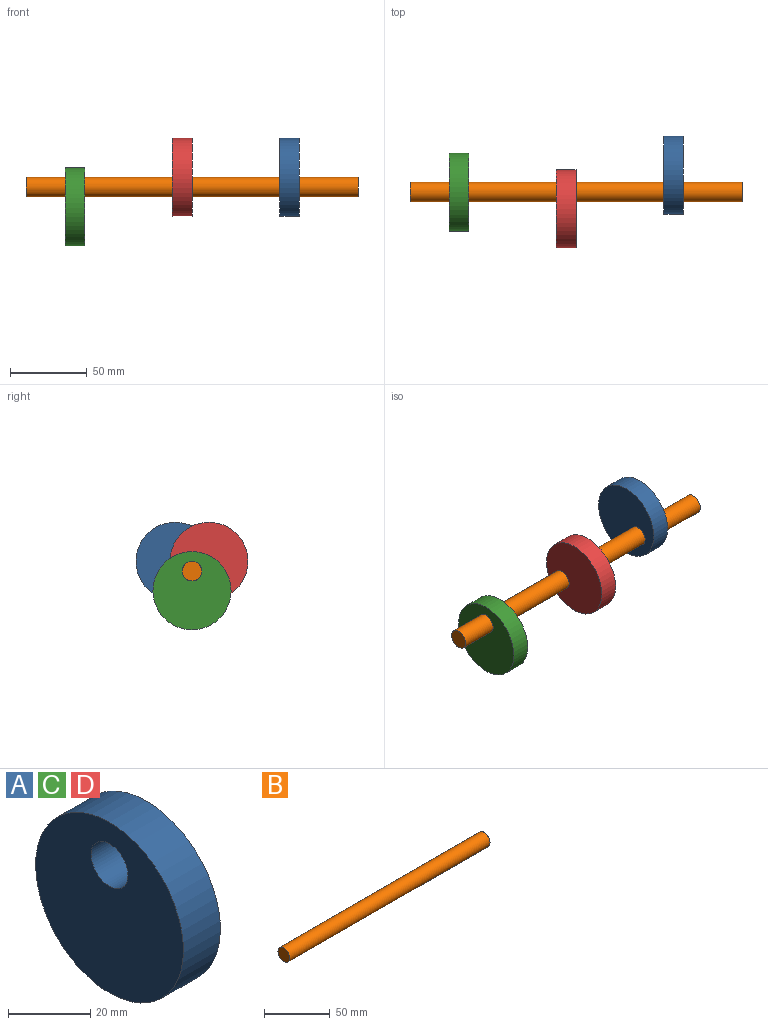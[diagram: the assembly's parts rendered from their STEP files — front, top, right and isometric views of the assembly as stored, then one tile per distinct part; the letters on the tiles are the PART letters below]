
ASSEMBLY  parts=4 mates=3
PART A: 4 faces, bbox 12.7x50.8x50.8 mm
  f0: plane 50.8x50.8mm, normal (1,0,0), area 1900.2mm2, adj f2,f3
  f1: plane 50.8x50.8mm, normal (-1,0,0), area 1900.2mm2, adj f2,f3
  f2: cylinder r=25.4mm len=50.8mm, axis (-1,0,0), area 2026.8mm2, adj f0,f1
  f3: cylinder r=6.35mm len=12.7mm, axis (-1,0,0), area 506.7mm2, adj f0,f1
PART B: 3 faces, bbox 215.9x12.7x12.7 mm
  f0: plane 12.7x12.7mm, normal (-1,0,0), area 126.7mm2, adj f2
  f1: plane 12.7x12.7mm, normal (1,0,0), area 126.7mm2, adj f2
  f2: cylinder r=6.35mm len=215.9mm, axis (-1,0,0), area 8614mm2, adj f0,f1
PART C: same geometry as A
PART D: same geometry as A
PLACE A rot(axis=(1,0,0),120deg) t=(133.35,49.49,28.58)mm
PLACE B t=(-6.35,0,-57.15)mm
PLACE C t=(-6.35,0,-57.15)mm
PLACE D rot(axis=(-1,0,0),120deg) t=(63.5,-49.49,28.57)mm
MATE fastened A.f3 <-> B.f2  axis (-1,0,0) through (63.5,0,0)mm
MATE fastened B.f2 <-> C.f3  axis (-1,0,0) through (-76.2,0,0)mm
MATE fastened B.f2 <-> D.f3  axis (-1,0,0) through (-6.35,0,0)mm
